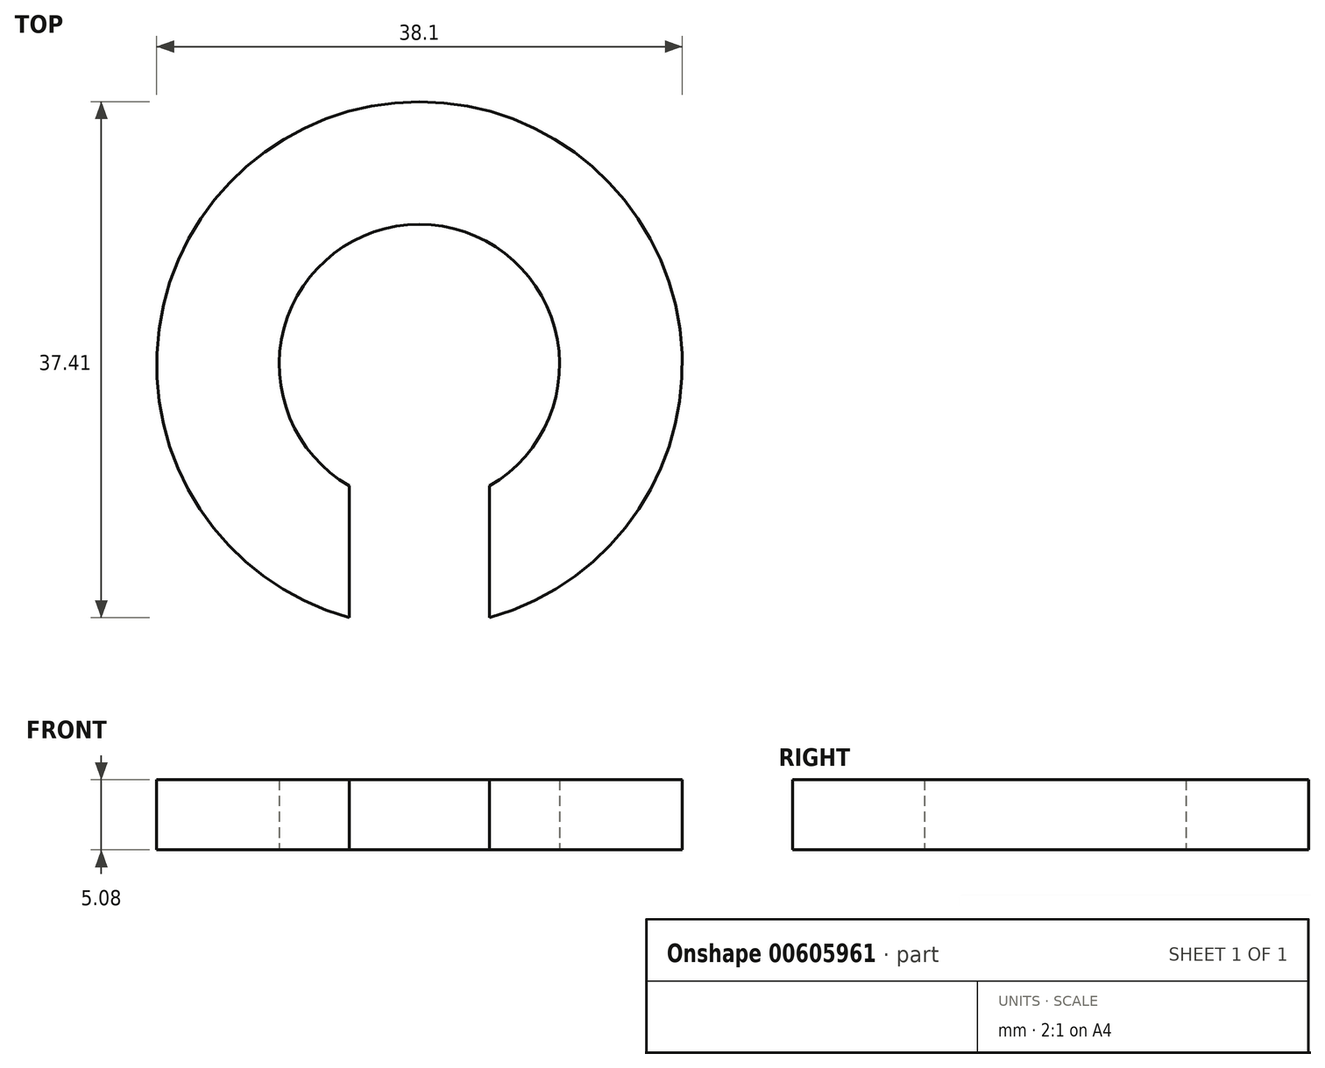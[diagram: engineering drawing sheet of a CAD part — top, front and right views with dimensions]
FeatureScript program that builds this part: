
annotation { "Feature Type Name" : "Feature", "Feature Type Description" : "" }
export const myFeature = defineFeature(function(context is Context, id is Id, definition is map)
    precondition{}
    {
        {
            var Q0;
            Q0=qCreatedBy(makeId("Top.planeOp"),FACE);
            var sketch = newSketch(context, id + "F0", { "sketchPlane" : qUnion([Q0])});
            skCircle(sketch, "E0", {"center": v(0, 0) * mm, "radius": 19.05 * mm});
            skCircle(sketch, "E1", {"center": v(0, 0) * mm, "radius": 10.16 * mm});
            skLineSegment(sketch, "E2", {"start": v(-5.08, -8.8) * mm, "end": v(-5.08, -18.36) * mm});
            skLineSegment(sketch, "E3", {"start": v(5.08, -8.8) * mm, "end": v(5.08, -18.36) * mm});
            skLineSegment(sketch, "E4", {"start": v(0, -19.05) * mm, "end": v(0, -10.16) * mm, "construction": true});
            skSolve(sketch);
        }
        {
            var Q0;
            {var subQ0=sQuery(id+"F0.wireOp",EDGE,"E2");Q0=makeQuery(id+"F0.imprint","IMPRINT",FACE,{"disambiguationData":[TD([[makeQuery(id+"F0.imprint","IMPRINT",EDGE,{"derivedFrom":subQ0}),-1.0]])]});}
            extrude(context, id + "F1", {"entities" : qUnion([Q0]), "depth" : 5.08 * mm, "offsetDistance" : 25.4 * mm});
        }
    });
